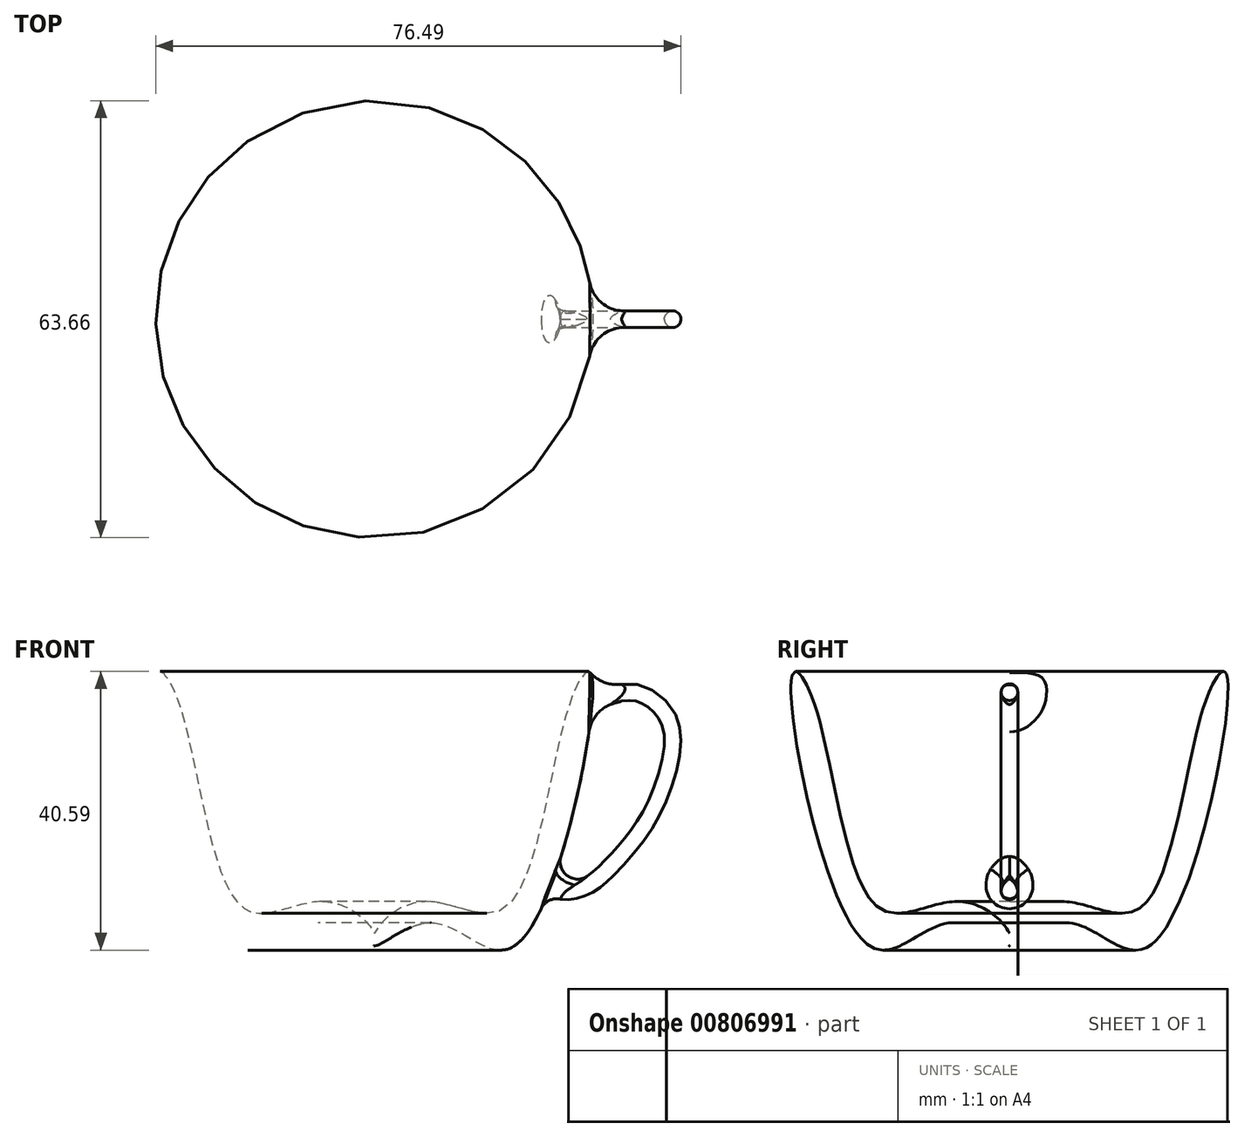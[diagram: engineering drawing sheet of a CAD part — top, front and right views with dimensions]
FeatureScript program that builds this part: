
annotation { "Feature Type Name" : "Feature", "Feature Type Description" : "" }
export const myFeature = defineFeature(function(context is Context, id is Id, definition is map)
    precondition{}
    {
        {
            var Q0;
            Q0=qCreatedBy(makeId("Front.planeOp"),FACE);
            var sketch = newSketch(context, id + "F0", { "sketchPlane" : qUnion([Q0])});
            skFitSpline(sketch, "E0", {"points": [v(0, 0) * mm, v(8.54, 3.36) * mm, v(20.42, 0) * mm, v(31.6, 39.52) * mm, v(28.36, 35.11) * mm, v(18.92, 5.45) * mm, v(7.46, 6.46) * mm, v(0, 1.86) * mm, v(0, 0) * mm]});
            skLineSegment(sketch, "E1", {"start": v(0, -22.59) * mm, "end": v(0, 48.19) * mm});
            skSolve(sketch);
        }
        {
            var Q0;
            {var subQ0=sQuery(id+"F0.wireOp",EDGE,"E1");var subQ1=sQuery(id+"F0.wireOp",EDGE,"E0");var subQ2=makeQuery(id+"F0.imprint","INTERSECT",VERTEX,{"disambiguationData":[OD(0.0)],"derivedFrom":[subQ1,subQ0]});Q0=makeQuery(id+"F0.imprint","IMPRINT",FACE,{"disambiguationData":[TD([[makeQuery(id+"F0.imprint","IMPRINT",EDGE,{"disambiguationData":[TD([[subQ2,-1.0]])],"derivedFrom":subQ1}),1.0]])]});}
            var Q1;
            Q1=sQuery(id+"F0.wireOp",EDGE,"E1");
            revolve(context, id + "F1", {"surfaceOperationType" : NewSurfaceOperationType.NEW, "entities" : qUnion([Q0]), "axis" : qUnion([Q1]), "revolveType" : RevolveType.FULL});
        }
        {
            var Q0;
            Q0=qCreatedBy(makeId("Front.planeOp"),FACE);
            var sketch = newSketch(context, id + "F2", { "sketchPlane" : qUnion([Q0])});
            skFitSpline(sketch, "E2", {"points": [v(29.06, 33.23) * mm, v(33.61, 36.11) * mm, v(37.83, 36.89) * mm, v(41.15, 35.22) * mm, v(43.37, 30.9) * mm, v(41.04, 20.8) * mm, v(37.27, 14.82) * mm, v(33.94, 11.16) * mm, v(31.28, 8.94) * mm, v(28.73, 8.05) * mm, v(26.74, 8.28) * mm, v(24.74, 10.6) * mm], "startDerivative": vector(45.7, 35.06) * mm, "endDerivative": vector(-25.22, 37.7) * mm});
            skSolve(sketch);
        }
        {
            var Q0;
            Q0=sQuery(id+"F2.wireOp",EDGE,"E2");
            var Q1;
            Q1=sQuery(id+"F2.wireOp",VERTEX,"E2.end");
            cPlane(context, id + "F3", {"entities" : qUnion([Q0, Q1]), "cplaneType" : CPlaneType.CURVE_POINT, "offset" : 25.4 * mm, "width" : 152.4 * mm, "height" : 152.4 * mm});
        }
        {
            var Q0;
            Q0=qCreatedBy(id+"F3.planeOp",FACE);
            var sketch = newSketch(context, id + "F4", { "sketchPlane" : qUnion([Q0])});
            skCircle(sketch, "E3", {"center": v(26.42, 0) * mm, "radius": 1.2 * mm});
            skSolve(sketch);
        }
        {
            var Q0;
            Q0=makeQuery(id+"F4.imprint","IMPRINT",FACE,{"disambiguationData":[TD([[makeQuery(id+"F4.imprint","IMPRINT",EDGE,{"derivedFrom":sQuery(id+"F4.wireOp",EDGE,"E3")}),1.0]])]});
            var Q1;
            Q1=sQuery(id+"F4.wireOp",EDGE,"E3");
            var Q2;
            Q2=sQuery(id+"F2.wireOp",EDGE,"E2");
            sweep(context, id + "F5", {"operationType" : NewBodyOperationType.ADD, "profiles" : qUnion([Q0]), "surfaceProfiles" : qUnion([Q1]), "path" : qUnion([Q2])});
        }
        {
            var Q0;
            Q0=makeQuery(id+"F5.boolean.opBoolean","INTERSECT",EDGE,{"disambiguationData":[OD(1.0)],"derivedFrom":[makeQuery(id+"F1.opRevolve","SWEPT_FACE",FACE,{"disambiguationData":[OSD([sQuery(id+"F0.wireOp",EDGE,"E0")])]}),makeQuery(id+"F5.opSweep","SWEPT_FACE",FACE,{"disambiguationData":[OSD([sQuery(id+"F2.wireOp",EDGE,"E2"),sQuery(id+"F4.wireOp",EDGE,"E3")])]})]});
            fillet(context, id + "F6", {"entities" : qUnion([Q0]), "radius" : 5.08 * mm, "tangentPropagation" : true, "allowEdgeOverflow" : false});
        }
        {
            var Q0;
            Q0=makeQuery(id+"F5.boolean.opBoolean","INTERSECT",EDGE,{"disambiguationData":[OD(0.0)],"derivedFrom":[makeQuery(id+"F1.opRevolve","SWEPT_FACE",FACE,{"disambiguationData":[OSD([sQuery(id+"F0.wireOp",EDGE,"E0")])]}),makeQuery(id+"F5.opSweep","SWEPT_FACE",FACE,{"disambiguationData":[OSD([sQuery(id+"F2.wireOp",EDGE,"E2"),sQuery(id+"F4.wireOp",EDGE,"E3")])]})]});
            fillet(context, id + "F7", {"entities" : qUnion([Q0]), "radius" : 2.54 * mm, "tangentPropagation" : true, "allowEdgeOverflow" : false});
        }
    });
